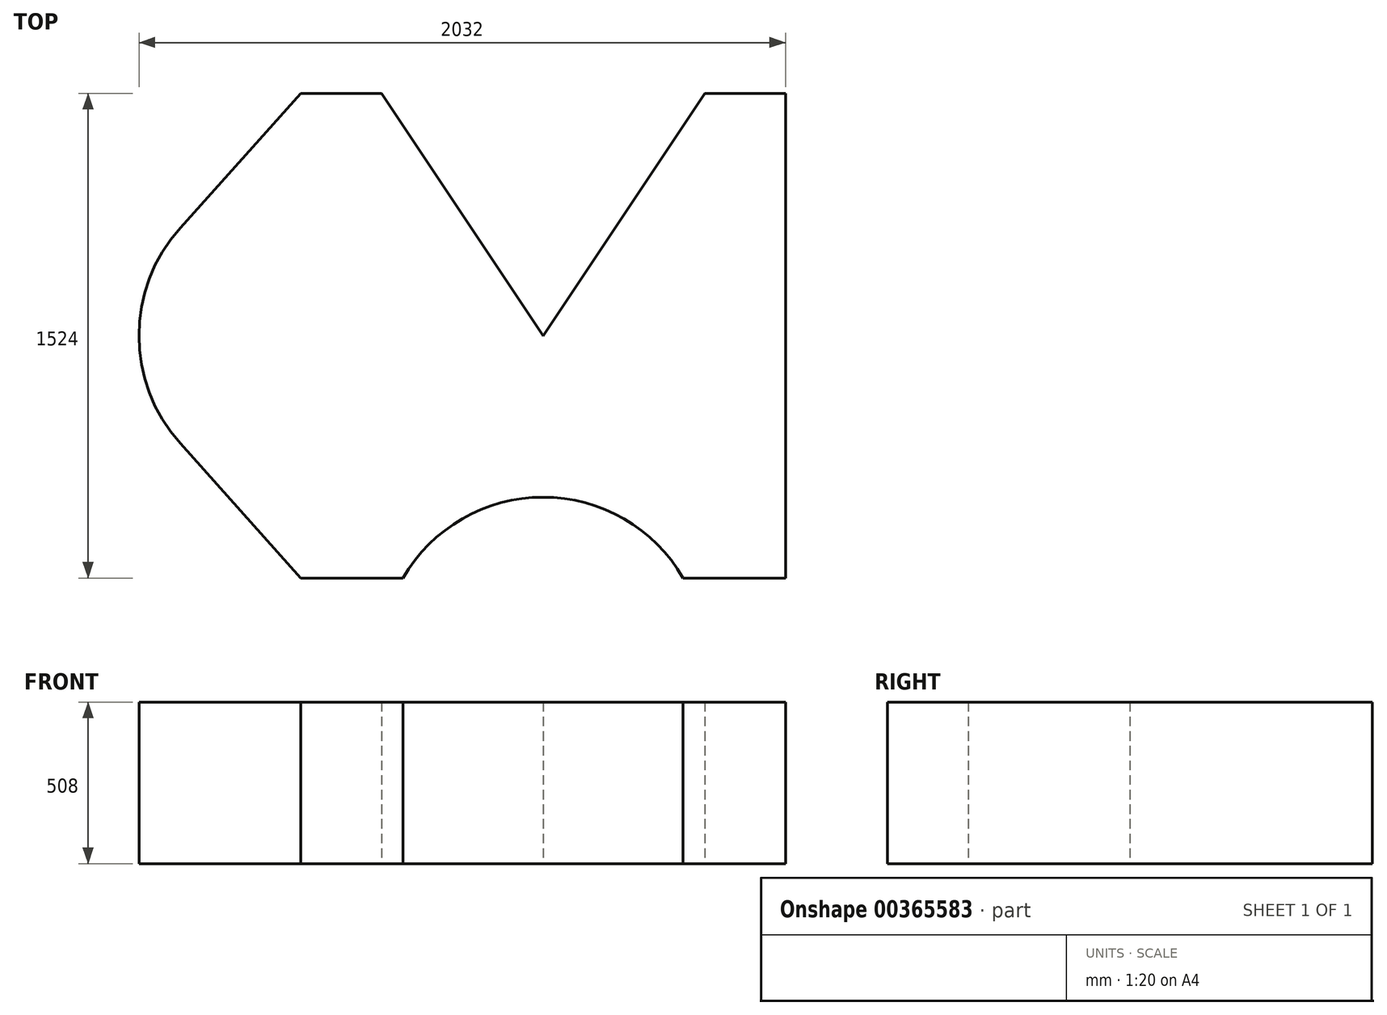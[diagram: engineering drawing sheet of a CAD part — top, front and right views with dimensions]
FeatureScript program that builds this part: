
annotation { "Feature Type Name" : "Feature", "Feature Type Description" : "" }
export const myFeature = defineFeature(function(context is Context, id is Id, definition is map)
    precondition{}
    {
        {
            var Q0;
            Q0=qCreatedBy(makeId("Top.planeOp"),FACE);
            var sketch = newSketch(context, id + "F0", { "sketchPlane" : qUnion([Q0])});
            skLineSegment(sketch, "E0", {"start": v(0, 0) * mm, "end": v(508, 762) * mm});
            skLineSegment(sketch, "E1", {"start": v(508, 762) * mm, "end": v(762, 762) * mm});
            skLineSegment(sketch, "E2", {"start": v(762, 762) * mm, "end": v(762, -762) * mm});
            skLineSegment(sketch, "E3", {"start": v(762, -762) * mm, "end": v(439.94, -762) * mm});
            skLineSegment(sketch, "E4", {"start": v(0, 0) * mm, "end": v(-508, 762) * mm});
            skLineSegment(sketch, "E5", {"start": v(-508, 762) * mm, "end": v(-762, 762) * mm});
            skLineSegment(sketch, "E6", {"start": v(-762, 762) * mm, "end": v(-1140.64, 338.67) * mm});
            skArc(sketch, "E7", {"start": v(439.94, -762) * mm, "mid": v(0, -508) * mm, "end": v(-439.94, -762) * mm});
            skLineSegment(sketch, "E8", {"start": v(-439.94, -762) * mm, "end": v(-762, -762) * mm});
            skLineSegment(sketch, "E9", {"start": v(-762, -762) * mm, "end": v(-1140.64, -338.67) * mm});
            skArc(sketch, "E10", {"start": v(-1140.64, 338.67) * mm, "mid": v(-1270, 0) * mm, "end": v(-1140.64, -338.67) * mm});
            skLineSegment(sketch, "E11", {"start": v(-490.22, 0) * mm, "end": v(668.87, 0) * mm, "construction": true});
            skLineSegment(sketch, "E12", {"start": v(0, 917.86) * mm, "end": v(0, -1051.61) * mm, "construction": true});
            skLineSegment(sketch, "E13", {"start": v(-762, 762) * mm, "end": v(-762, -967.67) * mm, "construction": true});
            skSolve(sketch);
        }
        {
            var Q0;
            Q0=makeQuery(id+"F0.imprint","IMPRINT",FACE,{"disambiguationData":[TD([[makeQuery(id+"F0.imprint","IMPRINT",EDGE,{"derivedFrom":sQuery(id+"F0.wireOp",EDGE,"E0")}),-1.0]])]});
            extrude(context, id + "F1", {"entities" : qUnion([Q0]), "depth" : 508 * mm});
        }
    });
